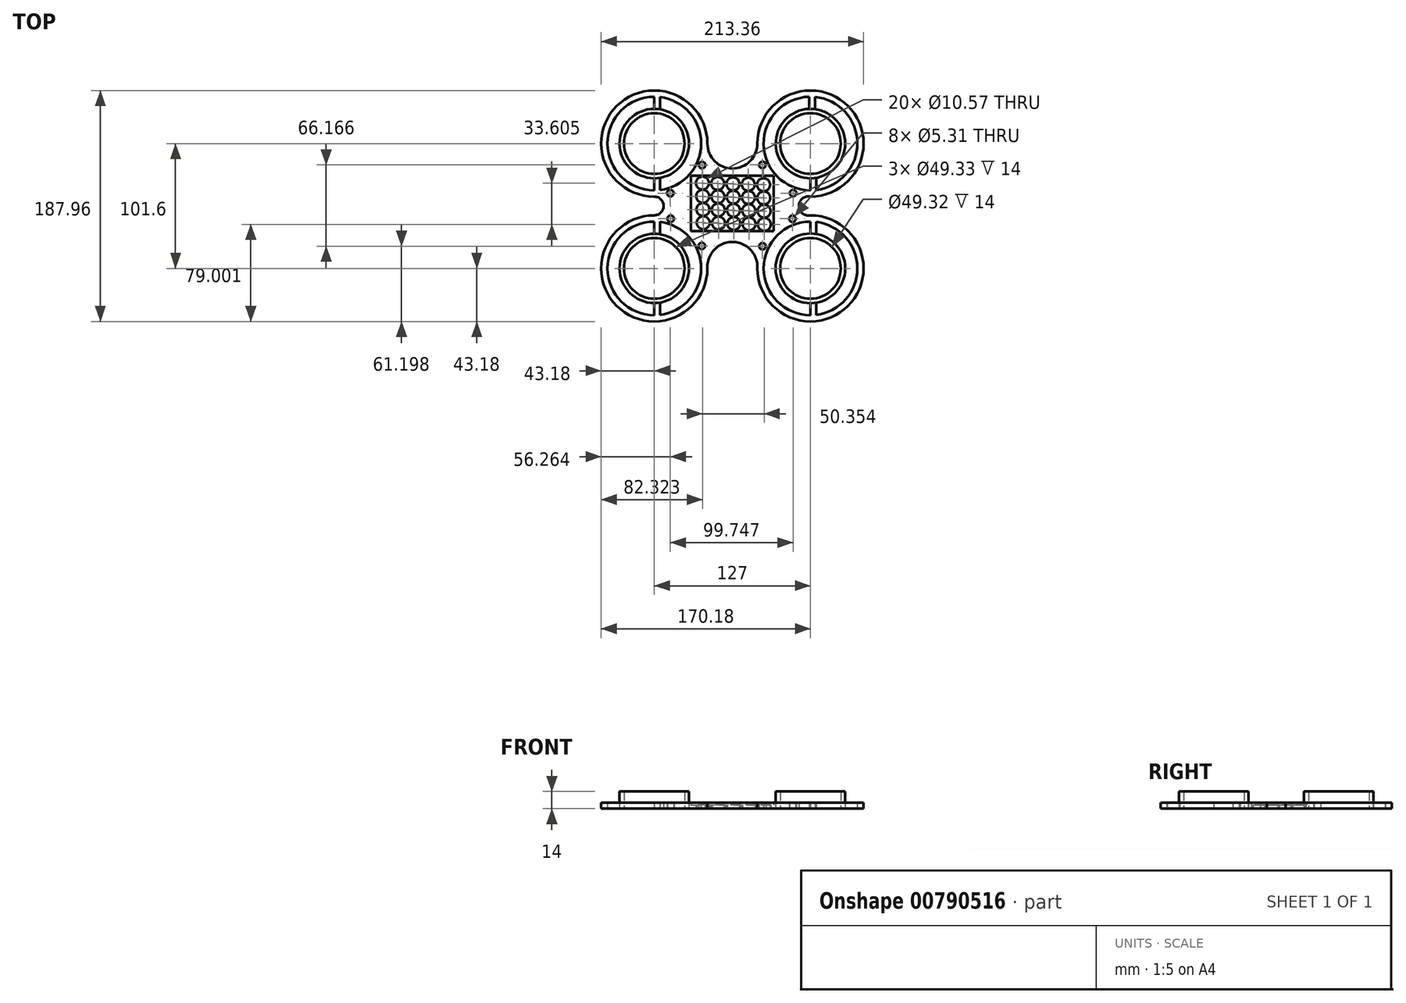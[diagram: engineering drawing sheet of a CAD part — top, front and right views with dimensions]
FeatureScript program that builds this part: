
annotation { "Feature Type Name" : "Feature", "Feature Type Description" : "" }
export const myFeature = defineFeature(function(context is Context, id is Id, definition is map)
    precondition{}
    {
        {
            var Q0;
            Q0=qCreatedBy(makeId("Top.planeOp"),FACE);
            var sketch = newSketch(context, id + "F0", { "sketchPlane" : qUnion([Q0])});
            skLineSegment(sketch, "E0.bottom", {"start": v(0, 101.6) * mm, "end": v(127, 101.6) * mm, "construction": true});
            skLineSegment(sketch, "E0.top", {"start": v(0, 0) * mm, "end": v(127, 0) * mm, "construction": true});
            skLineSegment(sketch, "E0.left", {"start": v(0, 101.6) * mm, "end": v(0, 0) * mm, "construction": true});
            skLineSegment(sketch, "E0.right", {"start": v(127, 101.6) * mm, "end": v(127, 0) * mm, "construction": true});
            skArc(sketch, "E1", {"start": v(127, 63.5) * mm, "mid": v(153.94, 128.54) * mm, "end": v(88.9, 101.6) * mm});
            skArc(sketch, "E2", {"start": v(88.9, 0) * mm, "mid": v(153.94, -26.94) * mm, "end": v(127, 38.1) * mm});
            skArc(sketch, "E3", {"start": v(38.1, 101.6) * mm, "mid": v(-26.94, 128.54) * mm, "end": v(0, 63.5) * mm});
            skArc(sketch, "E4", {"start": v(0, 38.1) * mm, "mid": v(-26.94, -26.94) * mm, "end": v(38.1, 0) * mm});
            skArc(sketch, "E5", {"start": v(127, 58.42) * mm, "mid": v(157.53, 132.13) * mm, "end": v(83.82, 101.6) * mm});
            skArc(sketch, "E6", {"start": v(43.18, 101.6) * mm, "mid": v(-30.53, 132.13) * mm, "end": v(0, 58.42) * mm});
            skArc(sketch, "E7", {"start": v(0, 43.18) * mm, "mid": v(-30.53, -30.53) * mm, "end": v(43.18, 0) * mm});
            skArc(sketch, "E8", {"start": v(83.82, 0) * mm, "mid": v(157.53, -30.53) * mm, "end": v(127, 43.18) * mm});
            skCircle(sketch, "E9", {"center": v(0, 101.6) * mm, "radius": 28.26 * mm});
            skCircle(sketch, "E10", {"center": v(127, 101.6) * mm, "radius": 28.25 * mm});
            skCircle(sketch, "E11", {"center": v(127, 0) * mm, "radius": 28.33 * mm});
            skCircle(sketch, "E12", {"center": v(0, 0) * mm, "radius": 28.2 * mm});
            skArc(sketch, "E13", {"start": v(38.1, 101.6) * mm, "mid": v(63.5, 76.2) * mm, "end": v(88.9, 101.6) * mm});
            skArc(sketch, "E14", {"start": v(43.18, 101.6) * mm, "mid": v(63.5, 81.28) * mm, "end": v(83.82, 101.6) * mm});
            skArc(sketch, "E15", {"start": v(127, 63.5) * mm, "mid": v(112.57, 50.8) * mm, "end": v(127, 38.1) * mm});
            skArc(sketch, "E16", {"start": v(0, 38.1) * mm, "mid": v(12.7, 50.8) * mm, "end": v(0, 63.5) * mm});
            skArc(sketch, "E17", {"start": v(88.9, 0) * mm, "mid": v(63.5, 26.59) * mm, "end": v(38.1, 0) * mm});
            skArc(sketch, "E18", {"start": v(0, 43.18) * mm, "mid": v(7.62, 50.8) * mm, "end": v(0, 58.42) * mm});
            skArc(sketch, "E19", {"start": v(83.82, 0) * mm, "mid": v(63.5, 21.51) * mm, "end": v(43.18, 0) * mm});
            skArc(sketch, "E20", {"start": v(127, 58.42) * mm, "mid": v(117.58, 50.8) * mm, "end": v(127, 43.18) * mm});
            skCircle(sketch, "E21", {"center": v(127, 0) * mm, "radius": 24.66 * mm});
            skCircle(sketch, "E22", {"center": v(127, 101.6) * mm, "radius": 24.66 * mm});
            skCircle(sketch, "E23", {"center": v(0, 101.6) * mm, "radius": 24.66 * mm});
            skCircle(sketch, "E24", {"center": v(0, 0) * mm, "radius": 24.66 * mm});
            skArc(sketch, "E25", {"start": v(38.1, 0) * mm, "mid": v(26.94, 26.94) * mm, "end": v(0, 38.1) * mm});
            skArc(sketch, "E26", {"start": v(127, 38.1) * mm, "mid": v(100.06, 26.94) * mm, "end": v(88.9, 0) * mm});
            skArc(sketch, "E27", {"start": v(88.9, 101.6) * mm, "mid": v(100.06, 74.66) * mm, "end": v(127, 63.5) * mm});
            skArc(sketch, "E28", {"start": v(0, 63.5) * mm, "mid": v(26.94, 74.66) * mm, "end": v(38.1, 101.6) * mm});
            skCircle(sketch, "E29", {"center": v(39.14, 69.43) * mm, "radius": 5.29 * mm});
            skLineSegment(sketch, "E30", {"start": v(126.12, 129.83) * mm, "end": v(126.12, 139.69) * mm});
            skLineSegment(sketch, "E31", {"start": v(130.67, 129.6) * mm, "end": v(130.67, 139.52) * mm});
            skLineSegment(sketch, "E32", {"start": v(127, 63.5) * mm, "end": v(127, 73.35) * mm});
            skLineSegment(sketch, "E33", {"start": v(131.54, 63.77) * mm, "end": v(131.54, 73.72) * mm});
            skLineSegment(sketch, "E34", {"start": v(0, 129.86) * mm, "end": v(0, 139.7) * mm});
            skLineSegment(sketch, "E35", {"start": v(0, 73.34) * mm, "end": v(0, 63.5) * mm});
            skLineSegment(sketch, "E36", {"start": v(4.55, 73.71) * mm, "end": v(4.55, 63.77) * mm});
            skLineSegment(sketch, "E37", {"start": v(0, 38.1) * mm, "end": v(0, 28.2) * mm});
            skLineSegment(sketch, "E38", {"start": v(4.55, 37.83) * mm, "end": v(4.55, 27.82) * mm});
            skLineSegment(sketch, "E39", {"start": v(0, -28.2) * mm, "end": v(0, -38.1) * mm});
            skLineSegment(sketch, "E40", {"start": v(4.55, -27.82) * mm, "end": v(4.55, -37.83) * mm});
            skLineSegment(sketch, "E41", {"start": v(127, -28.33) * mm, "end": v(127, -38.1) * mm});
            skLineSegment(sketch, "E42", {"start": v(131.55, -27.96) * mm, "end": v(131.55, -37.83) * mm});
            skLineSegment(sketch, "E43", {"start": v(127, 28.33) * mm, "end": v(127, 38.1) * mm});
            skLineSegment(sketch, "E44", {"start": v(131.55, 37.83) * mm, "end": v(131.55, 27.96) * mm});
            skLineSegment(sketch, "E45", {"start": v(4.55, 139.43) * mm, "end": v(4.55, 129.49) * mm});
            skCircle(sketch, "E46", {"center": v(87.98, 84.18) * mm, "radius": 2.66 * mm});
            skCircle(sketch, "E47", {"center": v(112.83, 61.26) * mm, "radius": 2.65 * mm});
            skCircle(sketch, "E48", {"center": v(112.34, 40.38) * mm, "radius": 2.65 * mm});
            skCircle(sketch, "E49", {"center": v(88.02, 18.02) * mm, "radius": 2.65 * mm});
            skCircle(sketch, "E50", {"center": v(38.63, 18.26) * mm, "radius": 2.65 * mm});
            skCircle(sketch, "E51", {"center": v(13.33, 40.38) * mm, "radius": 2.65 * mm});
            skCircle(sketch, "E52", {"center": v(13.08, 61.26) * mm, "radius": 2.65 * mm});
            skCircle(sketch, "E53", {"center": v(38.88, 84.1) * mm, "radius": 2.65 * mm});
            skLineSegment(sketch, "E54.bottom", {"start": v(29.77, 75.42) * mm, "end": v(97.23, 75.42) * mm});
            skLineSegment(sketch, "E54.top", {"start": v(29.77, 30.35) * mm, "end": v(97.23, 30.35) * mm});
            skLineSegment(sketch, "E54.left", {"start": v(29.77, 75.42) * mm, "end": v(29.77, 30.35) * mm});
            skLineSegment(sketch, "E54.right", {"start": v(97.23, 75.42) * mm, "end": v(97.23, 30.35) * mm});
            skCircle(sketch, "E55.0.1.0", {"center": v(39.37, 58.67) * mm, "radius": 5.29 * mm});
            skCircle(sketch, "E55.0.2.0", {"center": v(39.6, 47.92) * mm, "radius": 5.29 * mm});
            skCircle(sketch, "E55.0.3.0", {"center": v(39.82, 37.17) * mm, "radius": 5.29 * mm});
            skCircle(sketch, "E55.1.0.0", {"center": v(51.56, 69.09) * mm, "radius": 5.29 * mm});
            skCircle(sketch, "E55.1.1.0", {"center": v(51.79, 58.34) * mm, "radius": 5.29 * mm});
            skCircle(sketch, "E55.1.2.0", {"center": v(52.02, 47.58) * mm, "radius": 5.29 * mm});
            skCircle(sketch, "E55.1.3.0", {"center": v(52.24, 36.83) * mm, "radius": 5.29 * mm});
            skCircle(sketch, "E55.2.0.0", {"center": v(63.98, 68.75) * mm, "radius": 5.29 * mm});
            skCircle(sketch, "E55.2.1.0", {"center": v(64.2, 58) * mm, "radius": 5.29 * mm});
            skCircle(sketch, "E55.2.2.0", {"center": v(64.43, 47.25) * mm, "radius": 5.29 * mm});
            skCircle(sketch, "E55.2.3.0", {"center": v(64.66, 36.5) * mm, "radius": 5.29 * mm});
            skCircle(sketch, "E55.3.0.0", {"center": v(76.4, 68.41) * mm, "radius": 5.29 * mm});
            skCircle(sketch, "E55.3.1.0", {"center": v(76.63, 57.66) * mm, "radius": 5.29 * mm});
            skCircle(sketch, "E55.3.2.0", {"center": v(76.85, 46.9) * mm, "radius": 5.29 * mm});
            skCircle(sketch, "E55.3.3.0", {"center": v(77.08, 36.16) * mm, "radius": 5.29 * mm});
            skCircle(sketch, "E55.4.0.0", {"center": v(88.82, 68.08) * mm, "radius": 5.29 * mm});
            skCircle(sketch, "E55.4.1.0", {"center": v(89.04, 57.32) * mm, "radius": 5.29 * mm});
            skCircle(sketch, "E55.4.2.0", {"center": v(89.27, 46.57) * mm, "radius": 5.29 * mm});
            skCircle(sketch, "E55.4.3.0", {"center": v(89.5, 35.82) * mm, "radius": 5.29 * mm});
            skLineSegment(sketch, "E55.direction1", {"start": v(39.14, 69.43) * mm, "end": v(51.56, 69.09) * mm, "construction": true});
            skLineSegment(sketch, "E55.direction2", {"start": v(39.14, 69.43) * mm, "end": v(39.37, 58.67) * mm, "construction": true});
            skPoint(sketch, "E56.startSnap0", {"position": v(100.06, 26.94) * mm});
            skSolve(sketch);
        }
        {
            var Q0;
            Q0=makeQuery(id+"F0.imprint","IMPRINT",FACE,{"disambiguationData":[TD([[makeQuery(id+"F0.imprint","IMPRINT",EDGE,{"derivedFrom":sQuery(id+"F0.wireOp",EDGE,"E5")}),1.0]])]});
            var Q1;
            {var subQ0=sQuery(id+"F0.wireOp",EDGE,"E35");Q1=makeQuery(id+"F0.imprint","IMPRINT",FACE,{"disambiguationData":[TD([[makeQuery(id+"F0.imprint","IMPRINT",EDGE,{"derivedFrom":subQ0}),1.0]])]});}
            var Q2;
            {var subQ0=sQuery(id+"F0.wireOp",EDGE,"E34");Q2=makeQuery(id+"F0.imprint","IMPRINT",FACE,{"disambiguationData":[TD([[makeQuery(id+"F0.imprint","IMPRINT",EDGE,{"derivedFrom":subQ0}),-1.0]])]});}
            var Q3;
            {var subQ0=sQuery(id+"F0.wireOp",EDGE,"E37");Q3=makeQuery(id+"F0.imprint","IMPRINT",FACE,{"disambiguationData":[TD([[makeQuery(id+"F0.imprint","IMPRINT",EDGE,{"derivedFrom":subQ0}),1.0]])]});}
            var Q4;
            {var subQ0=sQuery(id+"F0.wireOp",EDGE,"E39");Q4=makeQuery(id+"F0.imprint","IMPRINT",FACE,{"disambiguationData":[TD([[makeQuery(id+"F0.imprint","IMPRINT",EDGE,{"derivedFrom":subQ0}),1.0]])]});}
            var Q5;
            {var subQ12=sQuery(id+"F0.wireOp",EDGE,"E13");Q5=makeQuery(id+"F0.imprint","IMPRINT",FACE,{"disambiguationData":[TD([[makeQuery(id+"F0.imprint","IMPRINT",EDGE,{"derivedFrom":subQ12}),-1.0]])]});}
            var Q6;
            {var subQ0=sQuery(id+"F0.wireOp",EDGE,"E30");Q6=makeQuery(id+"F0.imprint","IMPRINT",FACE,{"disambiguationData":[TD([[makeQuery(id+"F0.imprint","IMPRINT",EDGE,{"derivedFrom":subQ0}),-1.0]])]});}
            var Q7;
            {var subQ0=sQuery(id+"F0.wireOp",EDGE,"E32");Q7=makeQuery(id+"F0.imprint","IMPRINT",FACE,{"disambiguationData":[TD([[makeQuery(id+"F0.imprint","IMPRINT",EDGE,{"derivedFrom":subQ0}),-1.0]])]});}
            var Q8;
            {var subQ0=sQuery(id+"F0.wireOp",EDGE,"E43");Q8=makeQuery(id+"F0.imprint","IMPRINT",FACE,{"disambiguationData":[TD([[makeQuery(id+"F0.imprint","IMPRINT",EDGE,{"derivedFrom":subQ0}),-1.0]])]});}
            var Q9;
            {var subQ0=sQuery(id+"F0.wireOp",EDGE,"E41");Q9=makeQuery(id+"F0.imprint","IMPRINT",FACE,{"disambiguationData":[TD([[makeQuery(id+"F0.imprint","IMPRINT",EDGE,{"derivedFrom":subQ0}),1.0]])]});}
            extrude(context, id + "F1", {"entities" : qUnion([Q0, Q1, Q2, Q3, Q4, Q5, Q6, Q7, Q8, Q9]), "depth" : 5 * mm, "offsetDistance" : 25.4 * mm});
        }
        {
            var Q0;
            Q0=makeQuery(id+"F0.imprint","IMPRINT",FACE,{"disambiguationData":[TD([[makeQuery(id+"F0.imprint","IMPRINT",EDGE,{"derivedFrom":sQuery(id+"F0.wireOp",EDGE,"E24")}),-1.0]])]});
            var Q1;
            Q1=makeQuery(id+"F0.imprint","IMPRINT",FACE,{"disambiguationData":[TD([[makeQuery(id+"F0.imprint","IMPRINT",EDGE,{"derivedFrom":sQuery(id+"F0.wireOp",EDGE,"E23")}),-1.0]])]});
            var Q2;
            Q2=makeQuery(id+"F0.imprint","IMPRINT",FACE,{"disambiguationData":[TD([[makeQuery(id+"F0.imprint","IMPRINT",EDGE,{"derivedFrom":sQuery(id+"F0.wireOp",EDGE,"E22")}),-1.0]])]});
            var Q3;
            Q3=makeQuery(id+"F0.imprint","IMPRINT",FACE,{"disambiguationData":[TD([[makeQuery(id+"F0.imprint","IMPRINT",EDGE,{"derivedFrom":sQuery(id+"F0.wireOp",EDGE,"E21")}),-1.0]])]});
            extrude(context, id + "F2", {"entities" : qUnion([Q0, Q1, Q2, Q3]), "operationType" : NewBodyOperationType.ADD, "depth" : 4 * mm, "offsetDistance" : 25.4 * mm});
        }
        {
            var Q0;
            Q0=makeQuery(id+"F2.opExtrude","CAP_FACE",FACE,{"disambiguationData":[OSD([sQuery(id+"F0.wireOp",EDGE,"E9"),sQuery(id+"F0.wireOp",EDGE,"E23")])],"isStart":false});
            var Q1;
            Q1=makeQuery(id+"F2.opExtrude","CAP_FACE",FACE,{"disambiguationData":[OSD([sQuery(id+"F0.wireOp",EDGE,"E10"),sQuery(id+"F0.wireOp",EDGE,"E22")])],"isStart":false});
            var Q2;
            Q2=makeQuery(id+"F2.opExtrude","CAP_FACE",FACE,{"disambiguationData":[OSD([sQuery(id+"F0.wireOp",EDGE,"E11"),sQuery(id+"F0.wireOp",EDGE,"E21")])],"isStart":false});
            var Q3;
            Q3=makeQuery(id+"F2.opExtrude","CAP_FACE",FACE,{"disambiguationData":[OSD([sQuery(id+"F0.wireOp",EDGE,"E12"),sQuery(id+"F0.wireOp",EDGE,"E24")])],"isStart":false});
            extrude(context, id + "F3", {"entities" : qUnion([Q0, Q1, Q2, Q3]), "operationType" : NewBodyOperationType.ADD, "depth" : 10 * mm, "offsetDistance" : 25.4 * mm});
        }
        {
            var Q0;
            Q0=makeQuery(id+"F0.imprint","IMPRINT",FACE,{"disambiguationData":[TD([[makeQuery(id+"F0.imprint","IMPRINT",EDGE,{"derivedFrom":sQuery(id+"F0.wireOp",EDGE,"E29")}),-1.0]])]});
            extrude(context, id + "F4", {"entities" : qUnion([Q0]), "operationType" : NewBodyOperationType.ADD, "depth" : 3 * mm, "offsetDistance" : 25.4 * mm});
        }
    });
